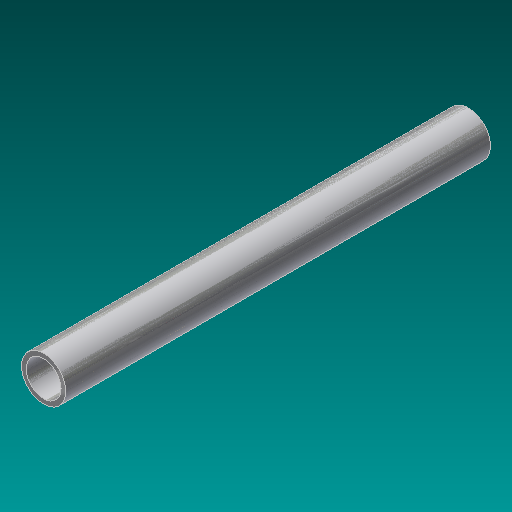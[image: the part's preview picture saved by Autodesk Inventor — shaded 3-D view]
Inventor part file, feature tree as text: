
AUTODESK INVENTOR PART (.ipt)
format: ipt  version: 2017 (Build 210142000, 142)  size: 120,832 bytes
history: native  units: in
note: dims shown in document units (in); Inventor stores cm internally (conversion verified against a paired STEP export)
features: extrude x1, sketch x1
ambient origin geometry x8: Origin, YZ Plane, XZ Plane, XY Plane, X Axis, Y Axis, Z Axis, Center Point
bodies: Solid1 (feature_tree)
feature tree (2):
  extrude  "Extrusion1"  Depth=18.25in
  sketch  "Sketch1"  dims[d0=1.9in d1=1.5in d2=18.25in d3=0.0in]
